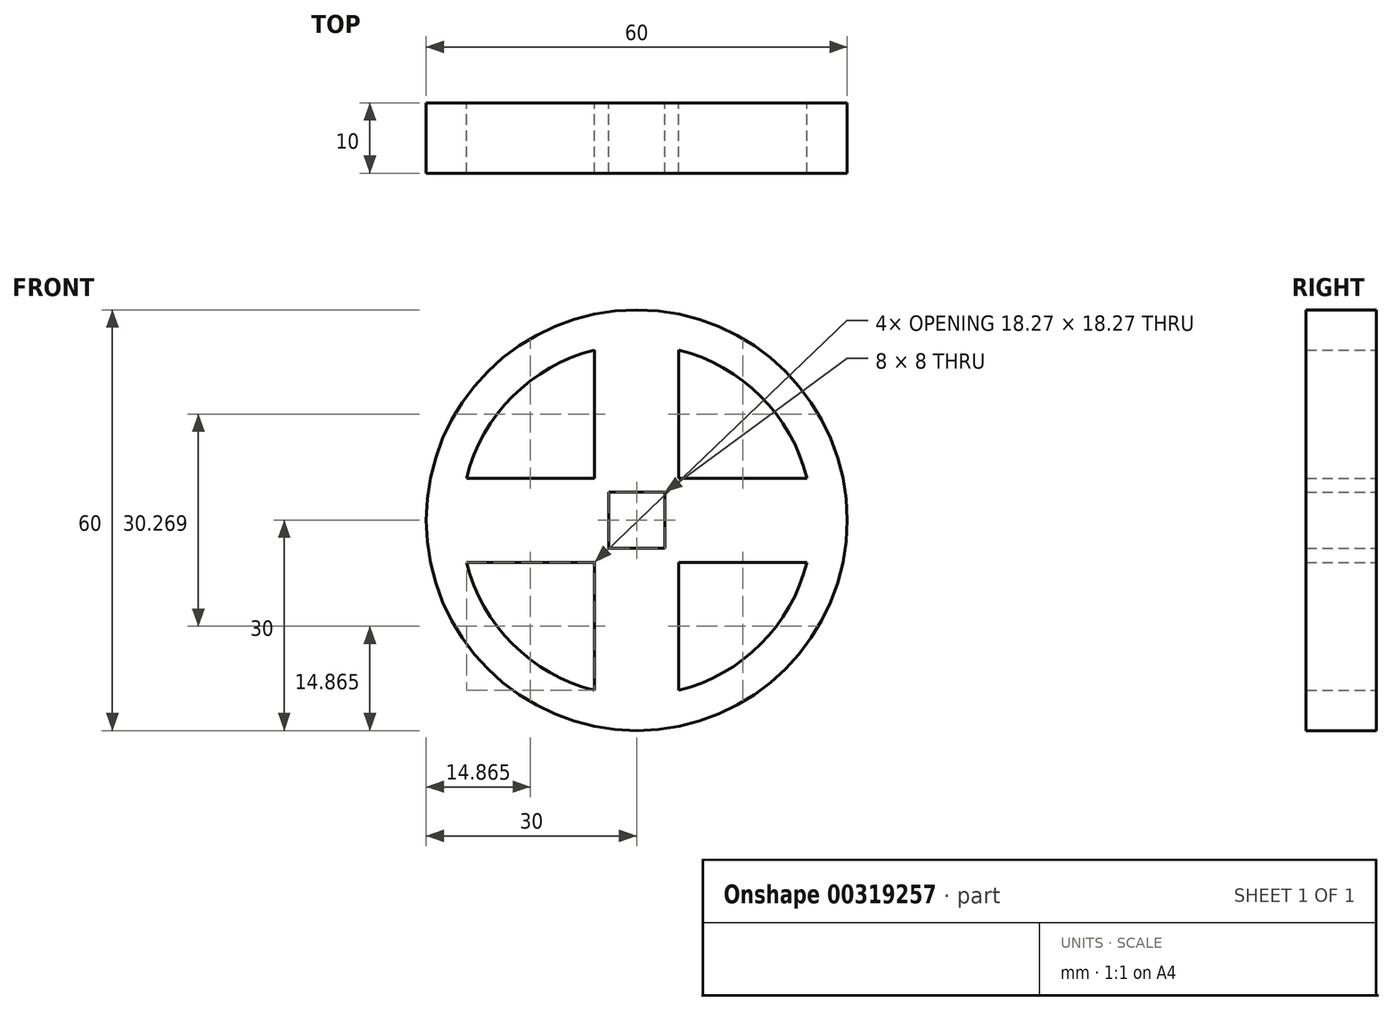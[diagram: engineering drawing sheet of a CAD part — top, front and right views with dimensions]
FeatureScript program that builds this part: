
annotation { "Feature Type Name" : "Feature", "Feature Type Description" : "" }
export const myFeature = defineFeature(function(context is Context, id is Id, definition is map)
    precondition{}
    {
        {
            var Q0;
            Q0=qCreatedBy(makeId("Front.planeOp"),FACE);
            var sketch = newSketch(context, id + "F0", { "sketchPlane" : qUnion([Q0])});
            skCircle(sketch, "E0", {"center": v(0, 0) * mm, "radius": 30 * mm});
            skArc(sketch, "E1", {"start": v(24.27, 6) * mm, "mid": v(17.68, 17.68) * mm, "end": v(6, 24.27) * mm});
            skLineSegment(sketch, "E2.bottom", {"start": v(24.27, 6) * mm, "end": v(6, 6) * mm});
            skLineSegment(sketch, "E2.top", {"start": v(24.27, -6) * mm, "end": v(6, -6) * mm});
            skLineSegment(sketch, "E3.left", {"start": v(-6, -24.27) * mm, "end": v(-6, -6) * mm});
            skLineSegment(sketch, "E3.right", {"start": v(6, -24.27) * mm, "end": v(6, -6) * mm});
            skArc(sketch, "E4.trimOffspring", {"start": v(6, -24.27) * mm, "mid": v(17.68, -17.68) * mm, "end": v(24.27, -6) * mm});
            skArc(sketch, "E5.trimOffspring", {"start": v(-24.27, -6) * mm, "mid": v(-17.68, -17.68) * mm, "end": v(-6, -24.27) * mm});
            skLineSegment(sketch, "E6.trimOffspring", {"start": v(6, 6) * mm, "end": v(6, 24.27) * mm});
            skLineSegment(sketch, "E7.trimOffspring", {"start": v(-6, 6) * mm, "end": v(-24.27, 6) * mm});
            skLineSegment(sketch, "E8.trimOffspring", {"start": v(-6, 6) * mm, "end": v(-6, 24.27) * mm});
            skLineSegment(sketch, "E9.trimOffspring", {"start": v(-6, -6) * mm, "end": v(-24.27, -6) * mm});
            skArc(sketch, "E10.trimOffspring", {"start": v(-6, 24.27) * mm, "mid": v(-17.68, 17.68) * mm, "end": v(-24.27, 6) * mm});
            skLineSegment(sketch, "E11.bottom", {"start": v(4, 4) * mm, "end": v(-4, 4) * mm});
            skLineSegment(sketch, "E11.top", {"start": v(4, -4) * mm, "end": v(-4, -4) * mm});
            skLineSegment(sketch, "E11.left", {"start": v(4, 4) * mm, "end": v(4, -4) * mm});
            skLineSegment(sketch, "E11.right", {"start": v(-4, 4) * mm, "end": v(-4, -4) * mm});
            skSolve(sketch);
        }
        {
            var Q0;
            Q0=makeQuery(id+"F0.imprint","IMPRINT",FACE,{"disambiguationData":[TD([[makeQuery(id+"F0.imprint","IMPRINT",EDGE,{"derivedFrom":sQuery(id+"F0.wireOp",EDGE,"E0")}),1.0]])]});
            extrude(context, id + "F1", {"entities" : qUnion([Q0]), "depth" : 10 * mm});
        }
    });
